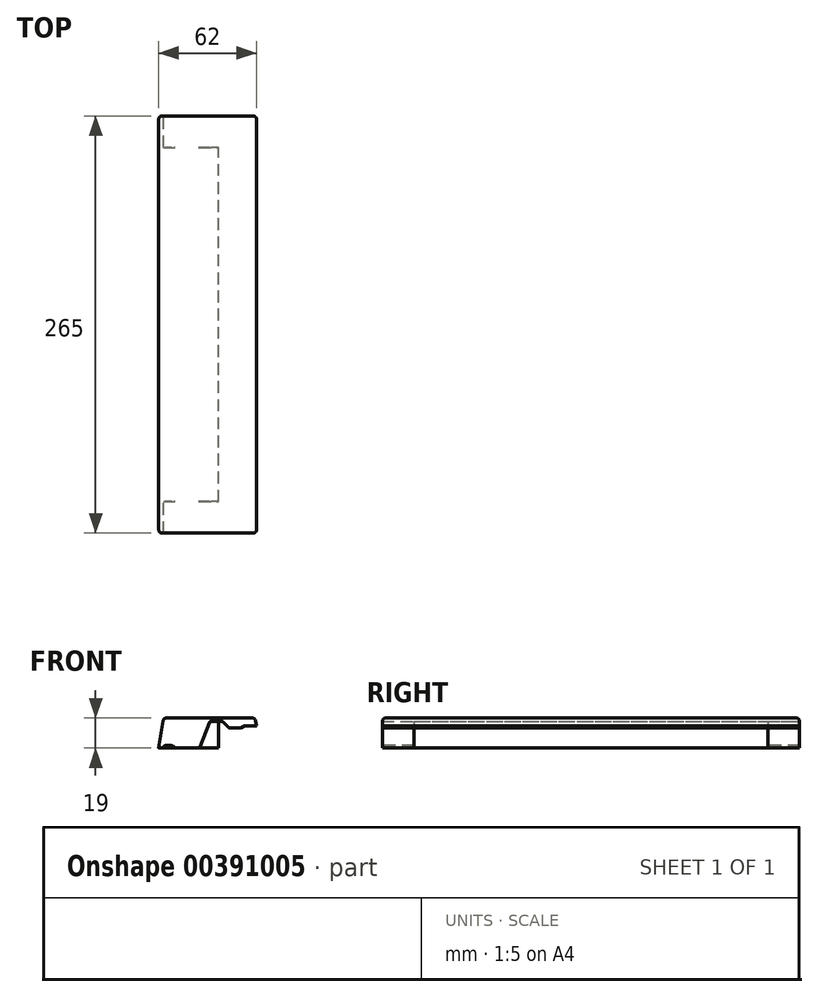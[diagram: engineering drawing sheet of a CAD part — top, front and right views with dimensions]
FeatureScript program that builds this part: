
annotation { "Feature Type Name" : "Feature", "Feature Type Description" : "" }
export const myFeature = defineFeature(function(context is Context, id is Id, definition is map)
    precondition{}
    {
        {
            var Q0;
            Q0=qCreatedBy(makeId("Front.planeOp"),FACE);
            var sketch = newSketch(context, id + "F0", { "sketchPlane" : qUnion([Q0])});
            skPoint(sketch, "E0.orphan", {"position": v(0, 0) * mm});
            skLineSegment(sketch, "E1", {"start": v(0, 1.5) * mm, "end": v(7, 1.5) * mm});
            skLineSegment(sketch, "E2", {"start": v(7, 1.5) * mm, "end": v(7, 0) * mm});
            skLineSegment(sketch, "E3", {"start": v(23, 0) * mm, "end": v(29.5, 17) * mm});
            skLineSegment(sketch, "E4", {"start": v(29.5, 17) * mm, "end": v(37.5, 17) * mm});
            skLineSegment(sketch, "E5", {"start": v(37.5, 17) * mm, "end": v(41.5, 12.7) * mm});
            skLineSegment(sketch, "E6", {"start": v(41.5, 12.7) * mm, "end": v(49, 12.7) * mm});
            skLineSegment(sketch, "E7", {"start": v(49, 12.7) * mm, "end": v(51, 14) * mm});
            skLineSegment(sketch, "E8", {"start": v(51, 14) * mm, "end": v(59, 14) * mm});
            skLineSegment(sketch, "E9", {"start": v(59, 14) * mm, "end": v(58.2, 19) * mm});
            skLineSegment(sketch, "E10", {"start": v(58.2, 19) * mm, "end": v(0, 19) * mm});
            skLineSegment(sketch, "E11", {"start": v(7, 0) * mm, "end": v(23, 0) * mm});
            skLineSegment(sketch, "E12", {"start": v(0, 1.5) * mm, "end": v(0, 0) * mm});
            skLineSegment(sketch, "E13", {"start": v(-3, 0) * mm, "end": v(0, 19) * mm});
            skLineSegment(sketch, "E14", {"start": v(0, 0) * mm, "end": v(-3, 0) * mm});
            skSolve(sketch);
        }
        {
            var Q0;
            Q0 = qSketchRegion(id + "F0", true);
            extrude(context, id + "F1", {"entities" : qUnion([Q0]), "depth" : 265 * mm});
        }
        {
            var Q0;
            Q0=makeQuery(id+"F1.opExtrude","SWEPT_EDGE",EDGE,{"disambiguationData":[OSD([sQuery(id+"F0.wireOp",EDGE,"E3"),sQuery(id+"F0.wireOp",EDGE,"E11")])]});
            var Q1;
            Q1=makeQuery(id+"F1.opExtrude","SWEPT_EDGE",EDGE,{"disambiguationData":[OSD([sQuery(id+"F0.wireOp",EDGE,"E5"),sQuery(id+"F0.wireOp",EDGE,"E6")])]});
            var Q2;
            Q2=makeQuery(id+"F1.opExtrude","SWEPT_EDGE",EDGE,{"disambiguationData":[OSD([sQuery(id+"F0.wireOp",EDGE,"E6"),sQuery(id+"F0.wireOp",EDGE,"E7")])]});
            var Q3;
            Q3=makeQuery(id+"F1.opExtrude","SWEPT_EDGE",EDGE,{"disambiguationData":[OSD([sQuery(id+"F0.wireOp",EDGE,"E7"),sQuery(id+"F0.wireOp",EDGE,"E8")])]});
            var Q4;
            Q4=makeQuery(id+"F1.opExtrude","SWEPT_EDGE",EDGE,{"disambiguationData":[OSD([sQuery(id+"F0.wireOp",EDGE,"E3"),sQuery(id+"F0.wireOp",EDGE,"E4")])]});
            var Q5;
            Q5=makeQuery(id+"F1.opExtrude","SWEPT_EDGE",EDGE,{"disambiguationData":[OSD([sQuery(id+"F0.wireOp",EDGE,"E4"),sQuery(id+"F0.wireOp",EDGE,"E5")])]});
            fillet(context, id + "F2", {"entities" : qUnion([Q0, Q1, Q2, Q3, Q4, Q5]), "radius" : 1 * mm, "tangentPropagation" : true, "allowEdgeOverflow" : false});
        }
        {
            var Q0;
            Q0=makeQuery(id+"F1.opExtrude","SWEPT_EDGE",EDGE,{"disambiguationData":[OSD([sQuery(id+"F0.wireOp",EDGE,"E1"),sQuery(id+"F0.wireOp",EDGE,"E2")])]});
            fillet(context, id + "F3", {"entities" : qUnion([Q0]), "radius" : 2 * mm, "tangentPropagation" : true, "allowEdgeOverflow" : false});
        }
        {
            var Q0;
            Q0=makeQuery(id+"F3.opFillet","BLEND_EDGE",EDGE,{"blendedFrom":[makeQuery(id+"F1.opExtrude","SWEPT_EDGE",EDGE,{"disambiguationData":[OSD([sQuery(id+"F0.wireOp",EDGE,"E1"),sQuery(id+"F0.wireOp",EDGE,"E2")])]}),makeQuery(id+"F1.opExtrude","SWEPT_FACE",FACE,{"disambiguationData":[OSD([sQuery(id+"F0.wireOp",EDGE,"E11")])]})],"blendedInto":[makeQuery(id+"F1.opExtrude","SWEPT_FACE",FACE,{"disambiguationData":[OSD([sQuery(id+"F0.wireOp",EDGE,"E11")])]})]});
            fillet(context, id + "F4", {"entities" : qUnion([Q0]), "radius" : 0.5 * mm, "tangentPropagation" : true, "allowEdgeOverflow" : false});
        }
        {
            var Q0;
            Q0=makeQuery(id+"F1.opExtrude","SWEPT_EDGE",EDGE,{"disambiguationData":[OSD([sQuery(id+"F0.wireOp",EDGE,"E1"),sQuery(id+"F0.wireOp",EDGE,"E12")])]});
            fillet(context, id + "F5", {"entities" : qUnion([Q0]), "radius" : 1 * mm, "tangentPropagation" : true, "allowEdgeOverflow" : false});
        }
        {
            var Q0;
            Q0=makeQuery(id+"F1.opExtrude","CAP_EDGE",EDGE,{"disambiguationData":[OSD([sQuery(id+"F0.wireOp",EDGE,"E10")])],"isStart":true});
            fillet(context, id + "F6", {"entities" : qUnion([Q0]), "radius" : 2 * mm, "tangentPropagation" : true, "allowEdgeOverflow" : false});
        }
        {
            var Q0;
            Q0=makeQuery(id+"F1.opExtrude","SWEPT_EDGE",EDGE,{"disambiguationData":[OSD([sQuery(id+"F0.wireOp",EDGE,"E10"),sQuery(id+"F0.wireOp",EDGE,"E13")])]});
            var Q1;
            Q1=makeQuery(id+"F1.opExtrude","SWEPT_EDGE",EDGE,{"disambiguationData":[OSD([sQuery(id+"F0.wireOp",EDGE,"E9"),sQuery(id+"F0.wireOp",EDGE,"E10")])]});
            var Q2;
            Q2=makeQuery(id+"F1.opExtrude","CAP_EDGE",EDGE,{"disambiguationData":[OSD([sQuery(id+"F0.wireOp",EDGE,"E13")])],"isStart":false});
            var Q3;
            Q3=makeQuery(id+"F1.opExtrude","CAP_EDGE",EDGE,{"disambiguationData":[OSD([sQuery(id+"F0.wireOp",EDGE,"E10")])],"isStart":false});
            var Q4;
            Q4=makeQuery(id+"F1.opExtrude","CAP_EDGE",EDGE,{"disambiguationData":[OSD([sQuery(id+"F0.wireOp",EDGE,"E9")])],"isStart":false});
            fillet(context, id + "F7", {"entities" : qUnion([Q0, Q1, Q2, Q3, Q4]), "radius" : 2 * mm, "tangentPropagation" : true, "allowEdgeOverflow" : false});
        }
        {
            var Q0;
            Q0=makeQuery(id+"F1.opExtrude","SWEPT_FACE",FACE,{"disambiguationData":[OSD([sQuery(id+"F0.wireOp",EDGE,"E14")])]});
            var sketch = newSketch(context, id + "F8", { "sketchPlane" : qUnion([Q0])});
            skLineSegment(sketch, "E15.bottom", {"start": v(-1, 20) * mm, "end": v(35, 20) * mm});
            skLineSegment(sketch, "E15.top", {"start": v(-1, 245) * mm, "end": v(35, 245) * mm});
            skLineSegment(sketch, "E15.left", {"start": v(-1, 20) * mm, "end": v(-1, 245) * mm});
            skLineSegment(sketch, "E15.right", {"start": v(35, 20) * mm, "end": v(35, 245) * mm});
            skSolve(sketch);
        }
        {
            var Q0;
            Q0 = qSketchRegion(id + "F8", true);
            extrude(context, id + "F9", {"entities" : qUnion([Q0]), "operationType" : NewBodyOperationType.ADD, "endBound" : BoundingType.UP_TO_NEXT, "oppositeDirection" : true, "depth" : 25 * mm});
        }
    });
